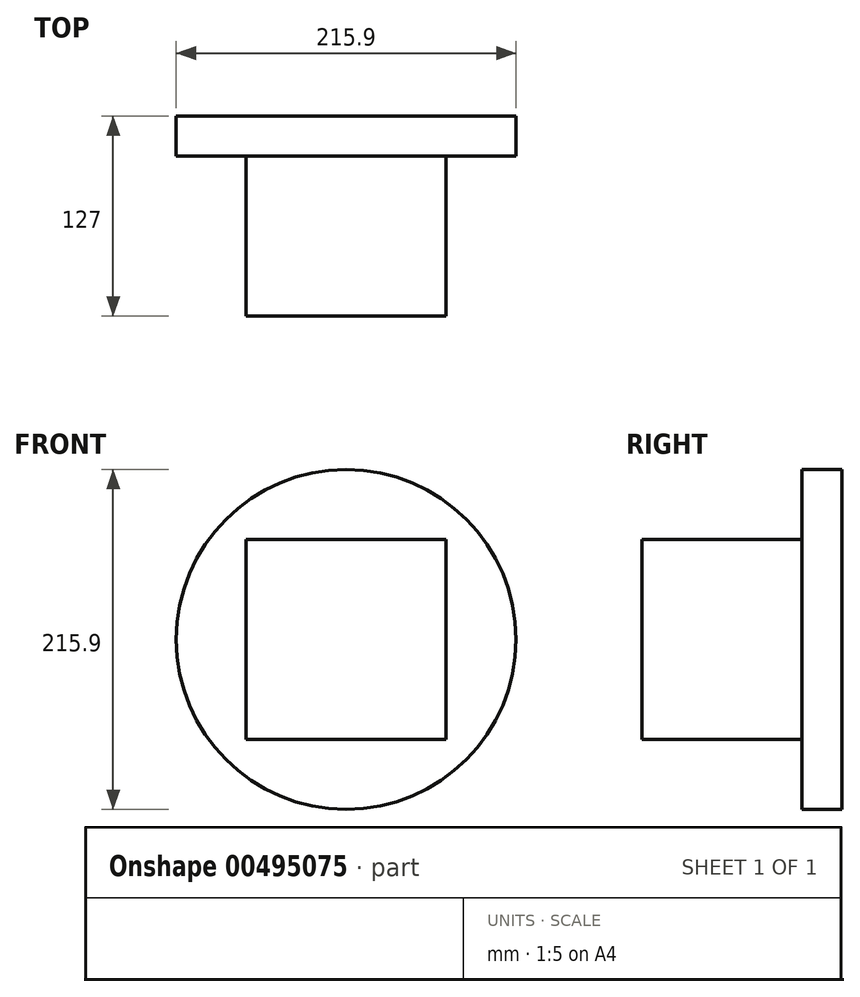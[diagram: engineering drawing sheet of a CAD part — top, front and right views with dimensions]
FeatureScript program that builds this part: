
annotation { "Feature Type Name" : "Feature", "Feature Type Description" : "" }
export const myFeature = defineFeature(function(context is Context, id is Id, definition is map)
    precondition{}
    {
        {
            var Q0;
            Q0=qCreatedBy(makeId("Front.planeOp"),FACE);
            var sketch = newSketch(context, id + "F0", { "sketchPlane" : qUnion([Q0])});
            skCircle(sketch, "E0", {"center": v(0, 0) * mm, "radius": 107.95 * mm});
            skSolve(sketch);
        }
        {
            var Q0;
            Q0 = qSketchRegion(id + "F0", true);
            extrude(context, id + "F1", {"entities" : qUnion([Q0]), "depth" : 25.4 * mm});
        }
        {
            var Q0;
            Q0=makeQuery(id+"F1.opExtrude","CAP_FACE",FACE,{"disambiguationData":[OSD([sQuery(id+"F0.wireOp",EDGE,"E0")])],"isStart":false});
            var sketch = newSketch(context, id + "F2", { "sketchPlane" : qUnion([Q0])});
            skLineSegment(sketch, "E1.bottom", {"start": v(-63.5, 63.5) * mm, "end": v(63.5, 63.5) * mm});
            skLineSegment(sketch, "E1.top", {"start": v(-63.5, -63.5) * mm, "end": v(63.5, -63.5) * mm});
            skLineSegment(sketch, "E1.left", {"start": v(-63.5, 63.5) * mm, "end": v(-63.5, -63.5) * mm});
            skLineSegment(sketch, "E1.right", {"start": v(63.5, 63.5) * mm, "end": v(63.5, -63.5) * mm});
            skSolve(sketch);
        }
        {
            var Q0;
            Q0=makeQuery(id+"F2.imprint","IMPRINT",FACE,{"disambiguationData":[TD([[makeQuery(id+"F2.imprint","IMPRINT",EDGE,{"derivedFrom":sQuery(id+"F2.wireOp",EDGE,"E1.bottom")}),-1.0]])]});
            extrude(context, id + "F3", {"entities" : qUnion([Q0]), "operationType" : NewBodyOperationType.ADD, "depth" : 101.6 * mm});
        }
    });
